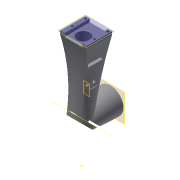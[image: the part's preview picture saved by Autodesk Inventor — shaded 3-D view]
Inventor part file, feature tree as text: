
AUTODESK INVENTOR PART (.ipt)
format: ipt  version: 2019.4 (Build 234330000, 330)  size: 442,368 bytes
history: native  units: mm
features: sketch x15, reference x12, extrude x10, other x7, plane x6, projected_geometry x3, loft x2
ambient origin geometry x8: Origin, YZ Plane, XZ Plane, XY Plane, X Axis, Y Axis, Z Axis, Center Point
bodies: Solid1 (feature_tree)
feature tree (55):
  plane  "Work Plane1"
  extrude  "Extrusion1"  Depth=4.0mm
  sketch  "Sketch2"  dims[d2=1.5mm d3=1.5mm]
  plane  "Work Plane2"
  loft  "Loft1"
  sketch  "Sketch4"  dims[d6=3.0mm d7=0.0mm d8=20.0mm]
  plane  "Work Plane3"
  loft  "Loft2"
  plane  "Work Plane4"
  extrude  "Extrusion2"  Depth=20.0mm
  extrude  "Extrusion3"  Depth=3.0mm TaperAngle=0.0deg
  extrude  "Extrusion4"  Depth=3.0mm TaperAngle=0.0deg
  extrude  "Extrusion5"  Depth=22.0mm
  sketch  "Sketch10"  dims[d31=5.0mm d32=0.0mm d35=0.0mm d36=90.0deg]
  plane  "Work Plane5"
  extrude  "Extrusion6"  Depth=20.0mm
  sketch  "Sketch11"  dims[d37=10.0mm d38=90.0deg d47=10.0mm d48=13.962634mm d49=0.0mm d50=90.0deg]
  plane  "Work Plane6"
  extrude  "Extrusion7"  TaperAngle=60.0deg  [1 undecoded]
  extrude  "Extrusion8"  TaperAngle=0.0deg  [1 undecoded]
  extrude  "Extrusion9"  Depth=10.0mm TaperAngle=0.0deg
  extrude  "Extrusion10"  Depth=5.0mm TaperAngle=0.0deg
  sketch  "Sketch1"  dims[d0=4.0mm d1=4.0mm]
  reference  "Reference1"
  projected_geometry  "Projected Loop1"
  projected_geometry  "Projected Loop2"
  sketch  "Sketch3"  dims[d4=1.5mm d5=1.5mm]
  reference  "Reference2"
  projected_geometry  "Projected Loop3"
  sketch  "Sketch5"  dims[d17=-3.0mm d18=3.0mm d19=0.0mm]
  reference  "Reference3"
  reference  "Reference4"
  sketch  "Sketch6"  dims[d20=16.0mm d21=3.0mm d22=0.0mm]
  reference  "Reference5"
  sketch  "Sketch7"  dims[d23=3.0mm d24=0.0mm d25=22.0mm]
  reference  "Reference6"
  sketch  "Sketch8"  dims[d26=5.0mm d27=0.0mm d28=20.0mm]
  sketch  "Sketch9"  dims[d29=60.0deg d30=60.0deg]
  reference  "Reference7"
  reference  "Reference8"
  sketch  "Sketch12"  dims[d51=5.0mm d52=0.0mm d53=5.0mm d54=0.0mm]
  reference  "Reference14"
  reference  "Reference15"
  sketch  "Sketch13"  dims[d55=1.5mm]
  sketch  "Sketch14"  dims[d56=24.0mm]
  reference  "Reference17"
  reference  "Reference18"
  sketch  "Sketch15"  dims[d57=3.0mm d58=14.0mm d59=5.0mm d60=0.0mm d61=10.0mm d62=0.0mm]
  other  "Assembly_Opentrons_Autofocus_v2.iam"
  other  "00_RasPi_Camera:1"
  other  "00_COMAR_Mirror_10mm:1"
  other  "00_objectivelens_10x:1"
  other  "07_OPENTRONS_Autofocus_objectivemount_v0:1"
  other  "01_Slide_camera_v1:1"
  other  "01_Slide_camera_flexure_v1:1"
note: 2 required parameter values undecoded (feature->parameter linkage not recoverable at this tier; creation-order binding heuristic only, values carry confidence <= 0.55)
